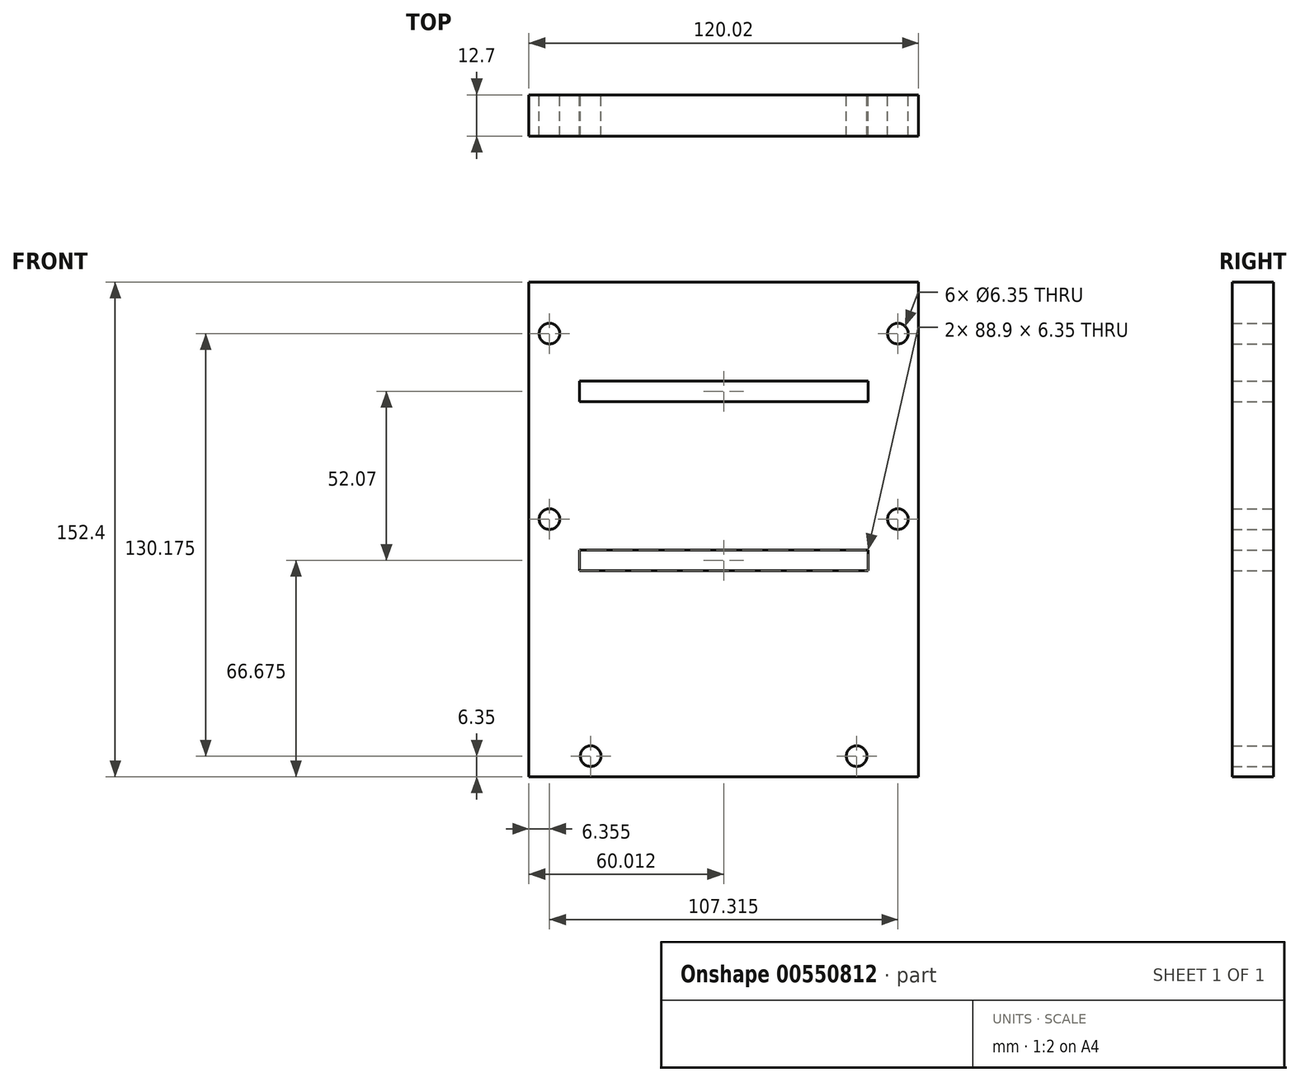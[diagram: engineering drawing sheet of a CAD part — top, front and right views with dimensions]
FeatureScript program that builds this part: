
annotation { "Feature Type Name" : "Feature", "Feature Type Description" : "" }
export const myFeature = defineFeature(function(context is Context, id is Id, definition is map)
    precondition{}
    {
        {
            var Q0;
            Q0=qCreatedBy(makeId("Front.planeOp"),FACE);
            var sketch = newSketch(context, id + "F0", { "sketchPlane" : qUnion([Q0])});
            skLineSegment(sketch, "E0.bottom", {"start": v(-120.01, 152.4) * mm, "end": v(0, 152.4) * mm});
            skLineSegment(sketch, "E0.top", {"start": v(-120.01, 0) * mm, "end": v(0, 0) * mm});
            skLineSegment(sketch, "E0.left", {"start": v(-120.01, 152.4) * mm, "end": v(-120.01, 0) * mm});
            skLineSegment(sketch, "E0.right", {"start": v(0, 152.4) * mm, "end": v(0, 0) * mm});
            skLineSegment(sketch, "E1", {"start": v(-120.02, 50.8) * mm, "end": v(0, 50.8) * mm, "construction": true});
            skLineSegment(sketch, "E2", {"start": v(-60, 152.4) * mm, "end": v(-60, 50.8) * mm, "construction": true});
            skCircle(sketch, "E3", {"center": v(-113.67, 136.53) * mm, "radius": 3.18 * mm});
            skCircle(sketch, "E4", {"center": v(-113.67, 79.38) * mm, "radius": 3.18 * mm});
            skCircle(sketch, "E5.MirrorC", {"center": v(-6.35, 79.38) * mm, "radius": 3.18 * mm});
            skCircle(sketch, "E6.MirrorC", {"center": v(-6.35, 136.53) * mm, "radius": 3.18 * mm});
            skCircle(sketch, "E7", {"center": v(-100.97, 6.35) * mm, "radius": 3.18 * mm});
            skCircle(sketch, "E8", {"center": v(-19.05, 6.35) * mm, "radius": 3.18 * mm});
            skLineSegment(sketch, "E9.bottom", {"start": v(-107.31, 139.7) * mm, "end": v(-12.7, 139.7) * mm, "construction": true});
            skLineSegment(sketch, "E9.top", {"start": v(-107.31, 12.7) * mm, "end": v(-12.7, 12.7) * mm, "construction": true});
            skLineSegment(sketch, "E9.left", {"start": v(-107.31, 139.7) * mm, "end": v(-107.31, 12.7) * mm, "construction": true});
            skLineSegment(sketch, "E9.right", {"start": v(-12.7, 139.7) * mm, "end": v(-12.7, 12.7) * mm, "construction": true});
            skLineSegment(sketch, "E10.bottom", {"start": v(-104.46, 121.92) * mm, "end": v(-15.56, 121.92) * mm});
            skLineSegment(sketch, "E10.top", {"start": v(-104.46, 115.57) * mm, "end": v(-15.56, 115.57) * mm});
            skLineSegment(sketch, "E10.left", {"start": v(-104.46, 121.92) * mm, "end": v(-104.46, 115.57) * mm});
            skLineSegment(sketch, "E10.right", {"start": v(-15.56, 121.92) * mm, "end": v(-15.56, 115.57) * mm});
            skLineSegment(sketch, "E11.bottom", {"start": v(-104.46, 69.85) * mm, "end": v(-15.56, 69.85) * mm});
            skLineSegment(sketch, "E11.top", {"start": v(-104.46, 63.5) * mm, "end": v(-15.56, 63.5) * mm});
            skLineSegment(sketch, "E11.left", {"start": v(-104.46, 69.85) * mm, "end": v(-104.46, 63.5) * mm});
            skLineSegment(sketch, "E11.right", {"start": v(-15.56, 69.85) * mm, "end": v(-15.56, 63.5) * mm});
            skSolve(sketch);
        }
        {
            var Q0;
            Q0=makeQuery(id+"F0.imprint","IMPRINT",FACE,{"disambiguationData":[TD([[makeQuery(id+"F0.imprint","IMPRINT",EDGE,{"derivedFrom":sQuery(id+"F0.wireOp",EDGE,"E0.bottom")}),-1.0]])]});
            extrude(context, id + "F1", {"entities" : qUnion([Q0]), "depth" : 12.7 * mm, "offsetDistance" : 25.4 * mm});
        }
    });
